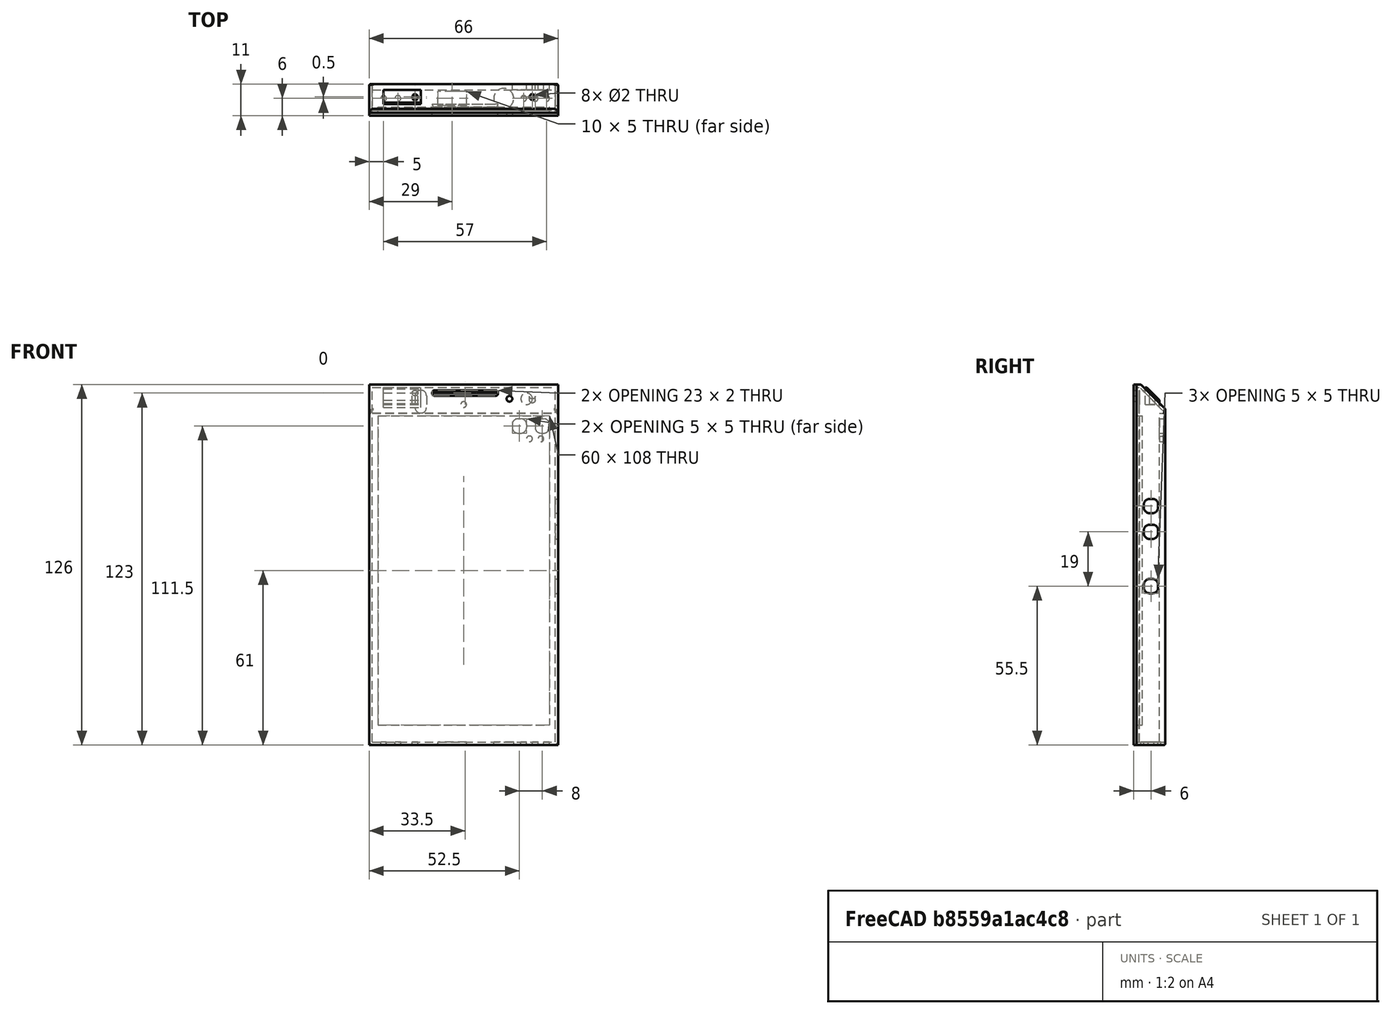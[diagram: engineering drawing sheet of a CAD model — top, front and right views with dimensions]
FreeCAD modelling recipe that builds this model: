
FCSTD DOCUMENT  (FreeCAD 0.15R4671 (Git))
Label: edge
License: All rights reserved
LicenseURL: http://es.wikipedia.org/wiki/Todos_los_derechos_reservados
objects: Part::Cut×29, Part::Box×16, Part::Cylinder×14, Part::Fillet×9, Part::Chamfer×2, Part::Thickness×1
note: 71 computed .brp shape members not serialized (recipe doc carries the construction recipe); baked Part::Feature solids carry a one-line shape summary decoded from their .brp

FEATURE [Part::Box] Box  label="Screen"
  Height = 108
  Length = 60
  Placement = pos=(2,-1,6) rot=(0,0,1;0rad)
  Width = 2
FEATURE [Part::Box] Box001  label="Edge-screen"
  Height = 124
  Length = 64
  Width = 9
FEATURE [Part::Chamfer] Chamfer
  Base = -> Box001
  Edges = 1 edges r=8.99: [Edge12]
FEATURE [Part::Cylinder] Cylinder  label="Cilindro"
  Angle = 360
  Height = 2
  Placement = pos=(32,2,118) rot=(0.57735,0.57735,-0.57735;2.0944rad)
  Radius = 1
FEATURE [Part::Thickness] Thickness
  Faces = -> Chamfer [Face5]
  Intersection = false
  Join = 2
  Mode = 0
  SelfIntersection = false
  Value = 1
FEATURE [Part::Box] Box002  label="Cubo"
  Height = 2
  Length = 23
  Placement = pos=(21,-2,121) rot=(0,0,1;0rad)
  Width = 10
FEATURE [Part::Fillet] Fillet
  Base = -> Box002
  Edges = 4 edges r=0.9: [Edge2,Edge4,Edge6,Edge8]
  Placement = pos=(0,-6,0) rot=(0,0,1;0rad)
FEATURE [Part::Cut] Cut
  Base = -> Thickness
  Tool = -> Fillet
FEATURE [Part::Cut] Cut001
  Base = -> Cut
  Tool = -> Cylinder
FEATURE [Part::Box] Box003  label="Cubo001"
  Height = 124
  Length = 64
  Placement = pos=(0,-10.2,0) rot=(0,0,1;0rad)
  Width = 10
FEATURE [Part::Cut] Cut002
  Base = -> Cut001
  Tool = -> Box003
FEATURE [Part::Box] Box004  label="Screen001"
  Height = 108
  Length = 60
  Placement = pos=(2,-1,6) rot=(0,0,1;0rad)
  Width = 2
FEATURE [Part::Cut] Cut003
  Base = -> Cut002
  Tool = -> Box
FEATURE [Part::Box] Box005  label="Cubo002"
  Height = 126
  Length = 66
  Placement = pos=(-1,-2,-1) rot=(0,0,1;0rad)
  Width = 1
FEATURE [Part::Cut] Cut004
  Base = -> Box005
  Tool = -> Cylinder
FEATURE [Part::Cut] Cut005
  Base = -> Cut004
  Tool = -> Fillet
FEATURE [Part::Box] Box007  label="Cubo003"
  Height = 5
  Length = 5
  Placement = pos=(-7,0,57) rot=(0,0,1;0rad)
  Width = 5
FEATURE [Part::Fillet] Fillet001
  Base = -> Box007
  Edges = 4 edges r=2: [Edge9,Edge10,Edge11,Edge12]
  Placement = pos=(69,1.5,23) rot=(0,0,1;0rad)
FEATURE [Part::Box] Box008  label="Cubo004"
  Height = 5
  Length = 5
  Placement = pos=(-7,0,57) rot=(0,0,1;0rad)
  Width = 5
FEATURE [Part::Fillet] Fillet002
  Base = -> Box008
  Edges = 4 edges r=2: [Edge9,Edge10,Edge11,Edge12]
  Placement = pos=(69,1.5,14) rot=(0,0,1;0rad)
FEATURE [Part::Box] Box009  label="Cubo005"
  Height = 5
  Length = 5
  Placement = pos=(-7,0,57) rot=(0,0,1;0rad)
  Width = 5
FEATURE [Part::Fillet] Fillet003
  Base = -> Box009
  Edges = 4 edges r=2: [Edge9,Edge10,Edge11,Edge12]
  Placement = pos=(69,1.5,-5) rot=(0,0,1;0rad)
FEATURE [Part::Cut] Cut006
  Base = -> Cut003
  Tool = -> Fillet002
FEATURE [Part::Cut] Cut007
  Base = -> Cut006
  Tool = -> Fillet001
FEATURE [Part::Cut] Cut008
  Base = -> Cut007
  Tool = -> Fillet003
FEATURE [Part::Box] Box011  label="Cubo007"
  Height = 13
  Length = 13
  Placement = pos=(4,2,112) rot=(0,0,1;0rad)
  Width = 5
FEATURE [Part::Cut] Cut012
  Base = -> Cut008
  Tool = -> Box011
FEATURE [Part::Cylinder] Cylinder001  label="Cilindro001"
  Angle = 360
  Height = 10
  Placement = pos=(48,3,120) rot=(0.57735,0.57735,-0.57735;2.0944rad)
  Radius = 1
FEATURE [Part::Cylinder] Cylinder002  label="Cilindro002"
  Angle = 360
  Height = 10
  Placement = pos=(54,2,120) rot=(0.57735,0.57735,-0.57735;2.0944rad)
  Radius = 2
FEATURE [Part::Cut] Cut014
  Base = -> Cut012
  Tool = -> Cylinder002
FEATURE [Part::Cut] Cut015
  Base = -> Cut014
  Tool = -> Cylinder001
FEATURE [Part::Cut] Cut016  label="Screen protector"
  Base = -> Cut005
  Tool = -> Cylinder001
FEATURE [Part::Box] Box013  label="Cubo009"
  Height = 5
  Length = 5
  Placement = pos=(57,6,108) rot=(0,0,1;0rad)
  Width = 5
FEATURE [Part::Fillet] Fillet004
  Base = -> Box013
  Edges = 4 edges r=2: [Edge2,Edge4,Edge6,Edge8]
FEATURE [Part::Box] Box014  label="Cubo010"
  Height = 5
  Length = 5
  Placement = pos=(57,6,108) rot=(0,0,1;0rad)
  Width = 5
FEATURE [Part::Fillet] Fillet005
  Base = -> Box014
  Edges = 4 edges r=2: [Edge2,Edge4,Edge6,Edge8]
  Placement = pos=(-8,0,0) rot=(0,0,1;0rad)
FEATURE [Part::Box] Box015  label="Cubo011"
  Height = 8
  Length = 4
  Placement = pos=(4,-5,116) rot=(0,0,1;0rad)
  Width = 5
FEATURE [Part::Fillet] Fillet006
  Base = -> Box015
  Edges = 4 edges r=1.99: [Edge2,Edge4,Edge6,Edge8]
  Placement = pos=(11,1,-1) rot=(0,0,1;0rad)
FEATURE [Part::Cut] Cut019
  Base = -> Cut015
  Tool = -> Fillet006
FEATURE [Part::Fillet] Fillet007
  Base = -> Cut019
  Edges = 4 edges r=1.5: [Edge140,Edge141,Edge168,Edge170]
FEATURE [Part::Box] Box016  label="Cubo012"
  Height = 115
  Length = 64
  Placement = pos=(0,7,0) rot=(0,0,1;0rad)
  Width = 2
FEATURE [Part::Cut] Cut020
  Base = -> Box016
  Tool = -> Fillet004
FEATURE [Part::Cut] Cut021
  Base = -> Cut020
  Tool = -> Fillet005
FEATURE [Part::Cut] Cut022
  Base = -> Fillet007
  Tool = -> Box011
FEATURE [Part::Box] Box017  label="Cubo013"
  Height = 6
  Length = 13
  Placement = pos=(4,2,118) rot=(0,0,1;0rad)
  Width = 5
FEATURE [Part::Chamfer] Chamfer001
  Base = -> Box017
  Edges = 1 edges r=4.5: [Edge12]
FEATURE [Part::Cylinder] Cylinder003  label="Cilindro003"
  Angle = 360
  Height = 10
  Placement = pos=(46,4,-6) rot=(0,0,1;0rad)
  Radius = 3.5
FEATURE [Part::Fillet] Fillet008
  Base = -> Cut022
  Edges = 4 edges r=0.5: [Edge1,Edge4,Edge5,Edge8]
FEATURE [Part::Cylinder] Cylinder004  label="Cilindro004"
  Angle = 360
  Height = 10
  Placement = pos=(53,4,-6) rot=(0,0,1;0rad)
  Radius = 1
FEATURE [Part::Cut] Cut023
  Base = -> Fillet008
  Tool = -> Cylinder003
FEATURE [Part::Cylinder] Cylinder005  label="Cilindro005"
  Angle = 360
  Height = 10
  Placement = pos=(57,4,-6) rot=(0,0,1;0rad)
  Radius = 1
FEATURE [Part::Cylinder] Cylinder006  label="Cilindro006"
  Angle = 360
  Height = 10
  Placement = pos=(61,4,-6) rot=(0,0,1;0rad)
  Radius = 1
FEATURE [Part::Cylinder] Cylinder007  label="Cilindro007"
  Angle = 360
  Height = 10
  Placement = pos=(15,4,-6) rot=(0,0,1;0rad)
  Radius = 1
FEATURE [Part::Cylinder] Cylinder008  label="Cilindro008"
  Angle = 360
  Height = 10
  Placement = pos=(9,4,-6) rot=(0,0,1;0rad)
  Radius = 1
FEATURE [Part::Cylinder] Cylinder009  label="Cilindro009"
  Angle = 360
  Height = 10
  Placement = pos=(4,4,-6) rot=(0,0,1;0rad)
  Radius = 1
FEATURE [Part::Cut] Cut024
  Base = -> Cut023
  Tool = -> Cylinder007
FEATURE [Part::Cut] Cut025
  Base = -> Cut024
  Tool = -> Cylinder008
FEATURE [Part::Cut] Cut026
  Base = -> Cut025
  Tool = -> Cylinder009
FEATURE [Part::Cut] Cut027
  Base = -> Cut026
  Tool = -> Cylinder004
FEATURE [Part::Cut] Cut028
  Base = -> Cut027
  Tool = -> Cylinder005
FEATURE [Part::Cut] Cut029
  Base = -> Cut028
  Tool = -> Cylinder006
FEATURE [Part::Cylinder] Cylinder010  label="Cilindro010"
  Angle = 360
  Height = 10
  Placement = pos=(15,4.5,113) rot=(0,0,1;0rad)
  Radius = 1
FEATURE [Part::Cut] Cut030  label="Sim"
  Base = -> Chamfer001
  Tool = -> Cylinder010
FEATURE [Part::Cylinder] Cylinder011  label="Cilindro011"
  Angle = 360
  Height = 10
  Placement = pos=(59,6,106) rot=(-0.57735,-0.57735,-0.57735;2.0944rad)
  Radius = 1
FEATURE [Part::Cylinder] Cylinder012  label="Cilindro012"
  Angle = 360
  Height = 10
  Placement = pos=(55,6,106) rot=(-0.57735,-0.57735,-0.57735;2.0944rad)
  Radius = 1
FEATURE [Part::Cut] Cut031
  Base = -> Cut021
  Tool = -> Cylinder012
FEATURE [Part::Cut] Cut032  label="Back"
  Base = -> Cut031
  Tool = -> Cylinder011
FEATURE [Part::Box] Box018  label="Cubo014"
  Height = 10
  Length = 10
  Placement = pos=(23,1.5,-3) rot=(0,0,1;0rad)
  Width = 5
FEATURE [Part::Cut] Cut033
  Base = -> Cut029
  Tool = -> Box018
FEATURE [Part::Cylinder] Cylinder013  label="Cilindro013"
  Angle = 360
  Height = 10
  Placement = pos=(56,4.5,113) rot=(0,0,1;0rad)
  Radius = 1
FEATURE [Part::Cut] Cut034  label="corver"
  Base = -> Cut033
  Tool = -> Cylinder013
